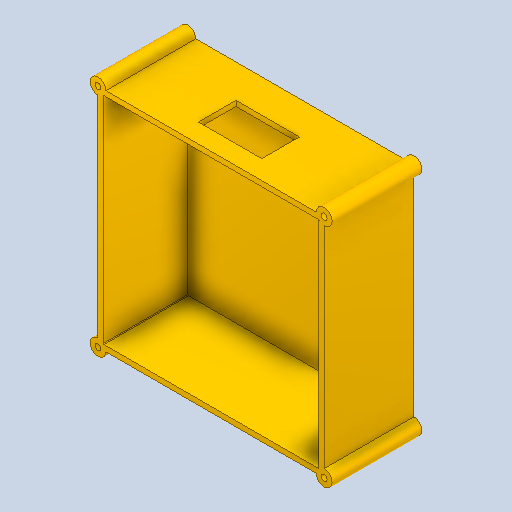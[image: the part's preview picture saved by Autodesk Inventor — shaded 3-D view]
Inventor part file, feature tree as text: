
AUTODESK INVENTOR PART (.ipt)
format: ipt  version: 2022 (Build 260153000, 153)  size: 194,560 bytes
history: native  units: in
note: dims shown in document units (in); Inventor stores cm internally (conversion verified against a paired STEP export)
features: extrude x4, sketch x4, shell x1
ambient origin geometry x8: Origin, YZ Plane, XZ Plane, XY Plane, X Axis, Y Axis, Z Axis, Center Point
bodies: Solid1 (feature_tree)
feature tree (9):
  extrude  "Extrusion1"  Depth=2.0in TaperAngle=0.0deg
  shell  "Shell1"  Thickness=0.125in
  extrude  "Extrusion2"  Depth=2.0in TaperAngle=0.0deg
  extrude  "Extrusion3"  Depth=1.5in
  extrude  "Extrusion4"  Depth=0.45in
  sketch  "Sketch1"  dims[d0=5.1in d1=2.0in d2=0.0in d3=0.125in]
  sketch  "Sketch2"  dims[d4=0.376in d5=2.0in d6=0.125in d7=0.0in d8=0.0in]
  sketch  "Sketch3"  dims[d10=4.25in d11=0.0in d12=1.5in]
  sketch  "Sketch4"  dims[d13=0.89in d14=0.45in d15=1.0in d16=0.0in d17=0.1417in]
